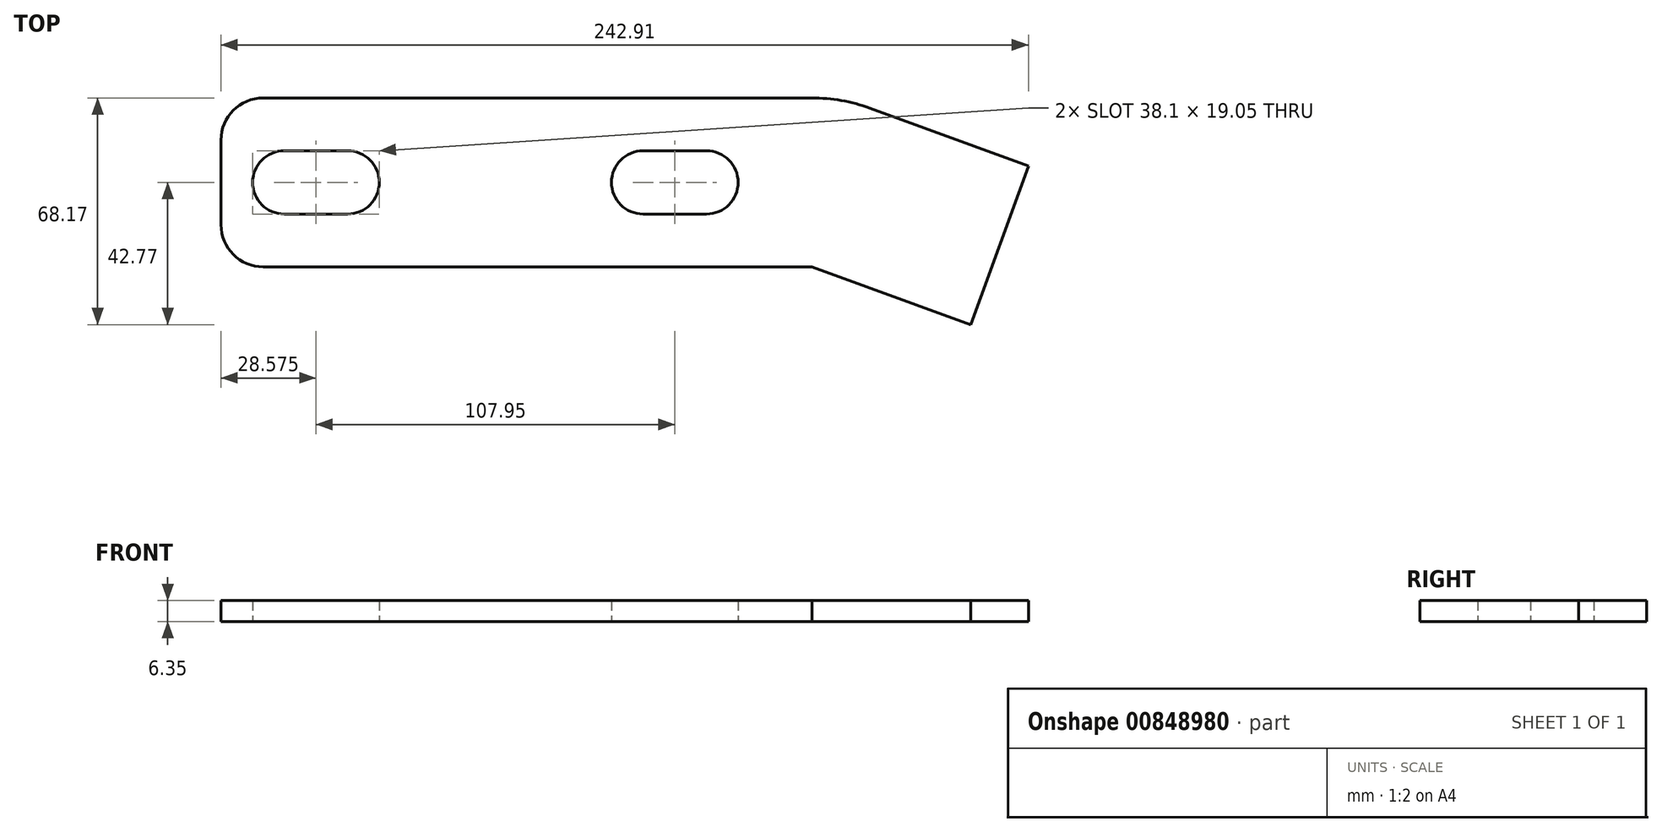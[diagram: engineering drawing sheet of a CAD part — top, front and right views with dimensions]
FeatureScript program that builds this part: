
annotation { "Feature Type Name" : "Feature", "Feature Type Description" : "" }
export const myFeature = defineFeature(function(context is Context, id is Id, definition is map)
    precondition{}
    {
        {
            var Q0;
            Q0=qCreatedBy(makeId("Top.planeOp"),FACE);
            var sketch = newSketch(context, id + "F0", { "sketchPlane" : qUnion([Q0])});
            skLineSegment(sketch, "E0.bottom", {"start": v(12.7, 0) * mm, "end": v(177.8, 0) * mm});
            skLineSegment(sketch, "E0.top", {"start": v(12.7, 50.8) * mm, "end": v(177.8, 50.8) * mm});
            skLineSegment(sketch, "E0.left", {"start": v(0, 12.7) * mm, "end": v(0, 38.1) * mm});
            skLineSegment(sketch, "E1", {"start": v(177.8, 0) * mm, "end": v(225.54, -17.37) * mm});
            skLineSegment(sketch, "E2.0", {"start": v(195.17, 47.74) * mm, "end": v(242.91, 30.36) * mm});
            skPoint(sketch, "E3.visualSharp", {"position": v(186.76, 50.8) * mm});
            skArc(sketch, "E3.filletArc", {"start": v(195.17, 47.74) * mm, "mid": v(186.62, 50.03) * mm, "end": v(177.8, 50.8) * mm});
            skLineSegment(sketch, "E4", {"start": v(225.54, -17.37) * mm, "end": v(242.91, 30.36) * mm});
            skArc(sketch, "E5", {"start": v(19.05, 34.93) * mm, "mid": v(9.53, 25.4) * mm, "end": v(19.05, 15.88) * mm});
            skPoint(sketch, "E5.centerSnap0", {"position": v(0, 25.4) * mm});
            skArc(sketch, "E6", {"start": v(38.1, 15.88) * mm, "mid": v(47.63, 25.4) * mm, "end": v(38.1, 34.93) * mm});
            skArc(sketch, "E7", {"start": v(127, 34.93) * mm, "mid": v(117.47, 25.4) * mm, "end": v(127, 15.88) * mm});
            skArc(sketch, "E8", {"start": v(146.05, 15.88) * mm, "mid": v(155.58, 25.4) * mm, "end": v(146.05, 34.93) * mm});
            skLineSegment(sketch, "E9", {"start": v(19.05, 34.92) * mm, "end": v(38.1, 34.92) * mm});
            skLineSegment(sketch, "E10", {"start": v(19.05, 15.88) * mm, "end": v(38.1, 15.88) * mm});
            skLineSegment(sketch, "E11", {"start": v(127, 15.88) * mm, "end": v(146.05, 15.88) * mm});
            skLineSegment(sketch, "E12", {"start": v(127, 34.93) * mm, "end": v(146.05, 34.93) * mm});
            skPoint(sketch, "E13.visualSharp", {"position": v(0, 50.8) * mm});
            skArc(sketch, "E13.filletArc", {"start": v(12.7, 50.8) * mm, "mid": v(3.72, 47.08) * mm, "end": v(0, 38.1) * mm});
            skPoint(sketch, "E14.visualSharp", {"position": v(0, 0) * mm});
            skArc(sketch, "E14.filletArc", {"start": v(0, 12.7) * mm, "mid": v(3.72, 3.72) * mm, "end": v(12.7, 0) * mm});
            skSolve(sketch);
        }
        {
            var Q0;
            Q0 = qSketchRegion(id + "F0", true);
            extrude(context, id + "F1", {"entities" : qUnion([Q0]), "depth" : 6.35 * mm, "offsetDistance" : 25.4 * mm});
        }
    });
